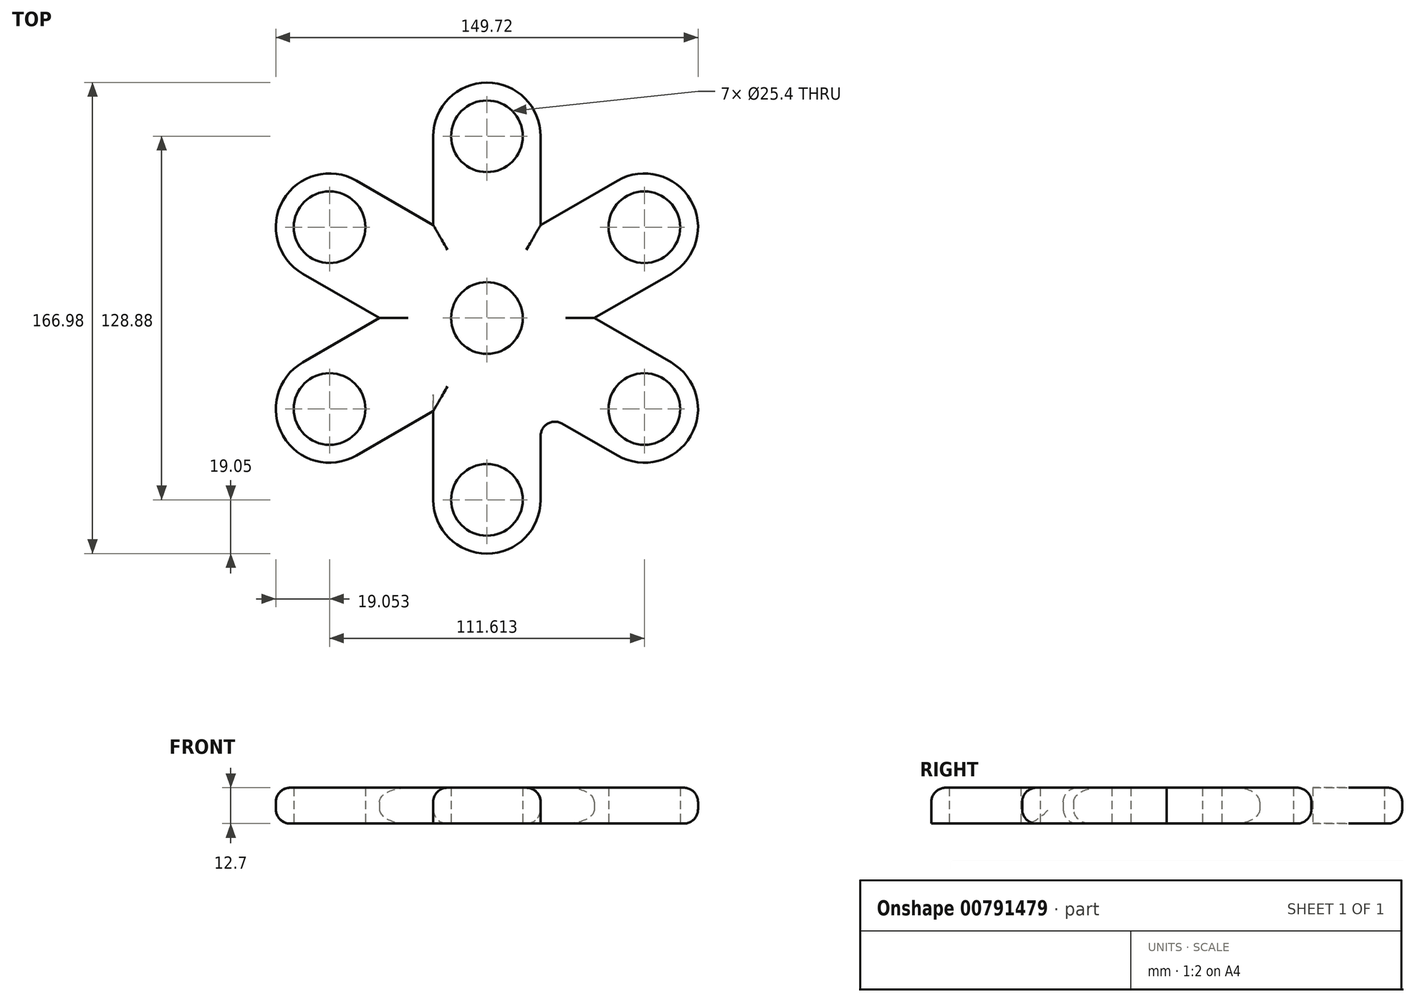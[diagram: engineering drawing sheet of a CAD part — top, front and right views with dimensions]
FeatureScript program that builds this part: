
annotation { "Feature Type Name" : "Feature", "Feature Type Description" : "" }
export const myFeature = defineFeature(function(context is Context, id is Id, definition is map)
    precondition{}
    {
        {
            var Q0;
            Q0=qCreatedBy(makeId("Top.planeOp"),FACE);
            var sketch = newSketch(context, id + "F0", { "sketchPlane" : qUnion([Q0])});
            skCircle(sketch, "E0", {"center": v(0, 0) * mm, "radius": 12.7 * mm});
            skCircle(sketch, "E1", {"center": v(0, 0) * mm, "radius": 19.05 * mm});
            skCircle(sketch, "E2", {"center": v(0, 64.44) * mm, "radius": 19.05 * mm});
            skCircle(sketch, "E3", {"center": v(0, 64.44) * mm, "radius": 12.7 * mm});
            skLineSegment(sketch, "E4", {"start": v(-19.05, 64.44) * mm, "end": v(-19.05, 0) * mm});
            skLineSegment(sketch, "E5", {"start": v(19.05, 64.44) * mm, "end": v(19.05, 0) * mm});
            skCircle(sketch, "E6.1.0", {"center": v(-55.8, 32.22) * mm, "radius": 12.7 * mm});
            skCircle(sketch, "E6.1.1", {"center": v(-55.8, 32.22) * mm, "radius": 19.05 * mm});
            skLineSegment(sketch, "E6.1.2", {"start": v(-46.28, 48.72) * mm, "end": v(9.53, 16.5) * mm});
            skLineSegment(sketch, "E6.1.3", {"start": v(-65.33, 15.72) * mm, "end": v(-9.52, -16.5) * mm});
            skCircle(sketch, "E6.2.0", {"center": v(-55.8, -32.22) * mm, "radius": 12.7 * mm});
            skCircle(sketch, "E6.2.1", {"center": v(-55.8, -32.22) * mm, "radius": 19.05 * mm});
            skLineSegment(sketch, "E6.2.2", {"start": v(-65.33, -15.72) * mm, "end": v(-9.52, 16.5) * mm});
            skLineSegment(sketch, "E6.2.3", {"start": v(-46.28, -48.72) * mm, "end": v(9.53, -16.5) * mm});
            skCircle(sketch, "E6.3.0", {"center": v(0, -64.44) * mm, "radius": 12.7 * mm});
            skCircle(sketch, "E6.3.1", {"center": v(0, -64.44) * mm, "radius": 19.05 * mm});
            skLineSegment(sketch, "E6.3.2", {"start": v(-19.05, -64.44) * mm, "end": v(-19.05, 0) * mm});
            skLineSegment(sketch, "E6.3.3", {"start": v(19.05, -64.44) * mm, "end": v(19.05, 0) * mm});
            skCircle(sketch, "E6.4.0", {"center": v(55.8, -32.22) * mm, "radius": 12.7 * mm});
            skCircle(sketch, "E6.4.1", {"center": v(55.8, -32.22) * mm, "radius": 19.05 * mm});
            skLineSegment(sketch, "E6.4.2", {"start": v(46.28, -48.72) * mm, "end": v(-9.53, -16.5) * mm});
            skLineSegment(sketch, "E6.4.3", {"start": v(65.33, -15.72) * mm, "end": v(9.52, 16.5) * mm});
            skCircle(sketch, "E6.5.0", {"center": v(55.8, 32.22) * mm, "radius": 12.7 * mm});
            skCircle(sketch, "E6.5.1", {"center": v(55.8, 32.22) * mm, "radius": 19.05 * mm});
            skLineSegment(sketch, "E6.5.2", {"start": v(65.33, 15.72) * mm, "end": v(9.53, -16.5) * mm});
            skLineSegment(sketch, "E6.5.3", {"start": v(46.28, 48.72) * mm, "end": v(-9.53, 16.5) * mm});
            skSolve(sketch);
        }
        {
            var Q0;
            Q0=makeQuery(id+"F0.imprint","IMPRINT",FACE,{"disambiguationData":[TD([[makeQuery(id+"F0.imprint","IMPRINT",EDGE,{"derivedFrom":sQuery(id+"F0.wireOp",EDGE,"E6.1.0")}),-1.0]])]});
            var Q1;
            {var subQ5=sQuery(id+"F0.wireOp",EDGE,"E6.1.2");var subQ6=sQuery(id+"F0.wireOp",EDGE,"E4");var subQ7=makeQuery(id+"F0.imprint","INTERSECT",VERTEX,{"derivedFrom":[subQ6,subQ5]});Q1=makeQuery(id+"F0.imprint","IMPRINT",FACE,{"disambiguationData":[TD([[makeQuery(id+"F0.imprint","IMPRINT",EDGE,{"disambiguationData":[TD([[subQ7,-1.0]])],"derivedFrom":subQ6}),-1.0]])]});}
            var Q2;
            {var subQ0=sQuery(id+"F0.wireOp",EDGE,"E6.1.2");var subQ1=sQuery(id+"F0.wireOp",EDGE,"E4");var subQ2=makeQuery(id+"F0.imprint","INTERSECT",VERTEX,{"derivedFrom":[subQ1,subQ0]});Q2=makeQuery(id+"F0.imprint","IMPRINT",FACE,{"disambiguationData":[TD([[makeQuery(id+"F0.imprint","IMPRINT",EDGE,{"disambiguationData":[TD([[subQ2,-1.0]])],"derivedFrom":subQ1}),1.0]])]});}
            var Q3;
            {var subQ1=sQuery(id+"F0.wireOp",EDGE,"E4");var subQ5=sQuery(id+"F0.wireOp",EDGE,"E2");var subQ6=makeQuery(id+"F0.imprint","INTERSECT",VERTEX,{"derivedFrom":[subQ5,subQ1]});Q3=makeQuery(id+"F0.imprint","IMPRINT",FACE,{"disambiguationData":[TD([[makeQuery(id+"F0.imprint","IMPRINT",EDGE,{"disambiguationData":[TD([[subQ6,-1.0]])],"derivedFrom":subQ5}),-1.0]])]});}
            var Q4;
            Q4=makeQuery(id+"F0.imprint","IMPRINT",FACE,{"disambiguationData":[TD([[makeQuery(id+"F0.imprint","IMPRINT",EDGE,{"derivedFrom":sQuery(id+"F0.wireOp",EDGE,"E3")}),-1.0]])]});
            var Q5;
            {var subQ5=sQuery(id+"F0.wireOp",EDGE,"E5");var subQ7=sQuery(id+"F0.wireOp",EDGE,"E6.5.3");var subQ9=makeQuery(id+"F0.imprint","INTERSECT",VERTEX,{"derivedFrom":[subQ5,subQ7]});Q5=makeQuery(id+"F0.imprint","IMPRINT",FACE,{"disambiguationData":[TD([[makeQuery(id+"F0.imprint","IMPRINT",EDGE,{"disambiguationData":[TD([[subQ9,-1.0]])],"derivedFrom":subQ5}),1.0]])]});}
            var Q6;
            Q6=makeQuery(id+"F0.imprint","IMPRINT",FACE,{"disambiguationData":[TD([[makeQuery(id+"F0.imprint","IMPRINT",EDGE,{"derivedFrom":sQuery(id+"F0.wireOp",EDGE,"E6.5.0")}),-1.0]])]});
            var Q7;
            {var subQ0=sQuery(id+"F0.wireOp",EDGE,"E6.5.3");var subQ1=sQuery(id+"F0.wireOp",EDGE,"E5");var subQ2=makeQuery(id+"F0.imprint","INTERSECT",VERTEX,{"derivedFrom":[subQ1,subQ0]});Q7=makeQuery(id+"F0.imprint","IMPRINT",FACE,{"disambiguationData":[TD([[makeQuery(id+"F0.imprint","IMPRINT",EDGE,{"disambiguationData":[TD([[subQ2,-1.0]])],"derivedFrom":subQ1}),-1.0]])]});}
            var Q8;
            {var subQ0=sQuery(id+"F0.wireOp",EDGE,"E5");var subQ3=sQuery(id+"F0.wireOp",EDGE,"E6.4.3");var subQ5=makeQuery(id+"F0.imprint","INTERSECT",VERTEX,{"derivedFrom":[subQ0,subQ3]});Q8=makeQuery(id+"F0.imprint","IMPRINT",FACE,{"disambiguationData":[TD([[makeQuery(id+"F0.imprint","IMPRINT",EDGE,{"disambiguationData":[TD([[subQ5,-1.0]])],"derivedFrom":subQ0}),-1.0]])]});}
            var Q9;
            {var subQ0=sQuery(id+"F0.wireOp",EDGE,"E6.1.2");var subQ3=sQuery(id+"F0.wireOp",EDGE,"E6.5.3");var subQ5=makeQuery(id+"F0.imprint","INTERSECT",VERTEX,{"derivedFrom":[subQ0,subQ3]});Q9=makeQuery(id+"F0.imprint","IMPRINT",FACE,{"disambiguationData":[TD([[makeQuery(id+"F0.imprint","IMPRINT",EDGE,{"disambiguationData":[TD([[subQ5,-1.0]])],"derivedFrom":subQ0}),-1.0]])]});}
            var Q10;
            {var subQ0=sQuery(id+"F0.wireOp",EDGE,"E4");var subQ3=sQuery(id+"F0.wireOp",EDGE,"E6.2.2");var subQ5=makeQuery(id+"F0.imprint","INTERSECT",VERTEX,{"derivedFrom":[subQ0,subQ3]});Q10=makeQuery(id+"F0.imprint","IMPRINT",FACE,{"disambiguationData":[TD([[makeQuery(id+"F0.imprint","IMPRINT",EDGE,{"disambiguationData":[TD([[subQ5,-1.0]])],"derivedFrom":subQ0}),1.0]])]});}
            var Q11;
            Q11=makeQuery(id+"F0.imprint","IMPRINT",FACE,{"disambiguationData":[TD([[makeQuery(id+"F0.imprint","IMPRINT",EDGE,{"derivedFrom":sQuery(id+"F0.wireOp",EDGE,"E0")}),-1.0]])]});
            var Q12;
            {var subQ0=sQuery(id+"F0.wireOp",EDGE,"E6.3.2");var subQ3=sQuery(id+"F0.wireOp",EDGE,"E6.1.3");var subQ5=makeQuery(id+"F0.imprint","INTERSECT",VERTEX,{"derivedFrom":[subQ3,subQ0]});Q12=makeQuery(id+"F0.imprint","IMPRINT",FACE,{"disambiguationData":[TD([[makeQuery(id+"F0.imprint","IMPRINT",EDGE,{"disambiguationData":[TD([[subQ5,-1.0]])],"derivedFrom":subQ3}),1.0]])]});}
            var Q13;
            {var subQ3=sQuery(id+"F0.wireOp",EDGE,"E6.2.2");var subQ5=sQuery(id+"F0.wireOp",EDGE,"E6.1.3");var subQ6=makeQuery(id+"F0.imprint","INTERSECT",VERTEX,{"derivedFrom":[subQ5,subQ3]});Q13=makeQuery(id+"F0.imprint","IMPRINT",FACE,{"disambiguationData":[TD([[makeQuery(id+"F0.imprint","IMPRINT",EDGE,{"disambiguationData":[TD([[subQ6,-1.0]])],"derivedFrom":subQ5}),1.0]])]});}
            var Q14;
            {var subQ5=sQuery(id+"F0.wireOp",EDGE,"E6.2.2");var subQ7=sQuery(id+"F0.wireOp",EDGE,"E6.1.3");var subQ9=makeQuery(id+"F0.imprint","INTERSECT",VERTEX,{"derivedFrom":[subQ7,subQ5]});Q14=makeQuery(id+"F0.imprint","IMPRINT",FACE,{"disambiguationData":[TD([[makeQuery(id+"F0.imprint","IMPRINT",EDGE,{"disambiguationData":[TD([[subQ9,-1.0]])],"derivedFrom":subQ7}),-1.0]])]});}
            var Q15;
            {var subQ3=sQuery(id+"F0.wireOp",EDGE,"E6.3.2");var subQ5=sQuery(id+"F0.wireOp",EDGE,"E6.2.3");var subQ6=makeQuery(id+"F0.imprint","INTERSECT",VERTEX,{"derivedFrom":[subQ5,subQ3]});Q15=makeQuery(id+"F0.imprint","IMPRINT",FACE,{"disambiguationData":[TD([[makeQuery(id+"F0.imprint","IMPRINT",EDGE,{"disambiguationData":[TD([[subQ6,-1.0]])],"derivedFrom":subQ5}),1.0]])]});}
            var Q16;
            {var subQ5=sQuery(id+"F0.wireOp",EDGE,"E6.3.2");var subQ7=sQuery(id+"F0.wireOp",EDGE,"E6.2.3");var subQ9=makeQuery(id+"F0.imprint","INTERSECT",VERTEX,{"derivedFrom":[subQ7,subQ5]});Q16=makeQuery(id+"F0.imprint","IMPRINT",FACE,{"disambiguationData":[TD([[makeQuery(id+"F0.imprint","IMPRINT",EDGE,{"disambiguationData":[TD([[subQ9,-1.0]])],"derivedFrom":subQ7}),-1.0]])]});}
            var Q17;
            {var subQ3=sQuery(id+"F0.wireOp",EDGE,"E6.4.2");var subQ5=sQuery(id+"F0.wireOp",EDGE,"E6.3.3");var subQ6=makeQuery(id+"F0.imprint","INTERSECT",VERTEX,{"derivedFrom":[subQ5,subQ3]});Q17=makeQuery(id+"F0.imprint","IMPRINT",FACE,{"disambiguationData":[TD([[makeQuery(id+"F0.imprint","IMPRINT",EDGE,{"disambiguationData":[TD([[subQ6,-1.0]])],"derivedFrom":subQ5}),1.0]])]});}
            var Q18;
            {var subQ5=sQuery(id+"F0.wireOp",EDGE,"E6.4.2");var subQ7=sQuery(id+"F0.wireOp",EDGE,"E6.3.3");var subQ9=makeQuery(id+"F0.imprint","INTERSECT",VERTEX,{"derivedFrom":[subQ7,subQ5]});Q18=makeQuery(id+"F0.imprint","IMPRINT",FACE,{"disambiguationData":[TD([[makeQuery(id+"F0.imprint","IMPRINT",EDGE,{"disambiguationData":[TD([[subQ9,-1.0]])],"derivedFrom":subQ7}),-1.0]])]});}
            var Q19;
            {var subQ3=sQuery(id+"F0.wireOp",EDGE,"E6.4.3");var subQ5=sQuery(id+"F0.wireOp",EDGE,"E6.5.2");var subQ6=makeQuery(id+"F0.imprint","INTERSECT",VERTEX,{"derivedFrom":[subQ3,subQ5]});Q19=makeQuery(id+"F0.imprint","IMPRINT",FACE,{"disambiguationData":[TD([[makeQuery(id+"F0.imprint","IMPRINT",EDGE,{"disambiguationData":[TD([[subQ6,-1.0]])],"derivedFrom":subQ3}),1.0]])]});}
            var Q20;
            {var subQ0=sQuery(id+"F0.wireOp",EDGE,"E6.3.3");var subQ3=sQuery(id+"F0.wireOp",EDGE,"E6.5.2");var subQ5=makeQuery(id+"F0.imprint","INTERSECT",VERTEX,{"derivedFrom":[subQ0,subQ3]});Q20=makeQuery(id+"F0.imprint","IMPRINT",FACE,{"disambiguationData":[TD([[makeQuery(id+"F0.imprint","IMPRINT",EDGE,{"disambiguationData":[TD([[subQ5,-1.0]])],"derivedFrom":subQ0}),1.0]])]});}
            var Q21;
            {var subQ0=sQuery(id+"F0.wireOp",EDGE,"E6.4.2");var subQ3=sQuery(id+"F0.wireOp",EDGE,"E6.2.3");var subQ5=makeQuery(id+"F0.imprint","INTERSECT",VERTEX,{"derivedFrom":[subQ3,subQ0]});Q21=makeQuery(id+"F0.imprint","IMPRINT",FACE,{"disambiguationData":[TD([[makeQuery(id+"F0.imprint","IMPRINT",EDGE,{"disambiguationData":[TD([[subQ5,-1.0]])],"derivedFrom":subQ3}),1.0]])]});}
            var Q22;
            Q22=makeQuery(id+"F0.imprint","IMPRINT",FACE,{"disambiguationData":[TD([[makeQuery(id+"F0.imprint","IMPRINT",EDGE,{"derivedFrom":sQuery(id+"F0.wireOp",EDGE,"E6.2.0")}),-1.0]])]});
            var Q23;
            Q23=makeQuery(id+"F0.imprint","IMPRINT",FACE,{"disambiguationData":[TD([[makeQuery(id+"F0.imprint","IMPRINT",EDGE,{"derivedFrom":sQuery(id+"F0.wireOp",EDGE,"E6.3.0")}),-1.0]])]});
            var Q24;
            Q24=makeQuery(id+"F0.imprint","IMPRINT",FACE,{"disambiguationData":[TD([[makeQuery(id+"F0.imprint","IMPRINT",EDGE,{"derivedFrom":sQuery(id+"F0.wireOp",EDGE,"E6.4.0")}),-1.0]])]});
            extrude(context, id + "F1", {"entities" : qUnion([Q0, Q1, Q2, Q3, Q4, Q5, Q6, Q7, Q8, Q9, Q10, Q11, Q12, Q13, Q14, Q15, Q16, Q17, Q18, Q19, Q20, Q21, Q22, Q23, Q24]), "depth" : 12.7 * mm, "offsetDistance" : 25.4 * mm});
        }
        {
            var Q0;
            Q0=makeQuery(id+"F1.opExtrude","CAP_EDGE",EDGE,{"disambiguationData":[OSD([sQuery(id+"F0.wireOp",EDGE,"E6.5.2")])],"isStart":false});
            var Q1;
            Q1=makeQuery(id+"F1.opExtrude","CAP_EDGE",EDGE,{"disambiguationData":[OSD([sQuery(id+"F0.wireOp",EDGE,"E5")])],"isStart":false});
            var Q2;
            Q2=makeQuery(id+"F1.opExtrude","CAP_EDGE",EDGE,{"disambiguationData":[OSD([sQuery(id+"F0.wireOp",EDGE,"E6.1.2")])],"isStart":false});
            var Q3;
            Q3=makeQuery(id+"F1.opExtrude","CAP_EDGE",EDGE,{"disambiguationData":[OSD([sQuery(id+"F0.wireOp",EDGE,"E6.2.2")])],"isStart":false});
            var Q4;
            Q4=makeQuery(id+"F1.opExtrude","CAP_EDGE",EDGE,{"disambiguationData":[OSD([sQuery(id+"F0.wireOp",EDGE,"E6.3.2")])],"isStart":false});
            var Q5;
            Q5=makeQuery(id+"F1.opExtrude","CAP_EDGE",EDGE,{"disambiguationData":[OSD([sQuery(id+"F0.wireOp",EDGE,"E6.4.2")])],"isStart":false});
            var Q6;
            Q6=makeQuery(id+"F1.opExtrude","SWEPT_FACE",FACE,{"disambiguationData":[OSD([sQuery(id+"F0.wireOp",EDGE,"E6.4.2")])]});
            var Q7;
            Q7=makeQuery(id+"F1.opExtrude","CAP_EDGE",EDGE,{"disambiguationData":[OSD([sQuery(id+"F0.wireOp",EDGE,"E6.2.2")])],"isStart":true});
            var Q8;
            Q8=makeQuery(id+"F1.opExtrude","CAP_EDGE",EDGE,{"disambiguationData":[OSD([sQuery(id+"F0.wireOp",EDGE,"E6.5.3")])],"isStart":true});
            var Q9;
            Q9=makeQuery(id+"F1.opExtrude","CAP_EDGE",EDGE,{"disambiguationData":[OSD([sQuery(id+"F0.wireOp",EDGE,"E6.1.3")])],"isStart":true});
            var Q10;
            Q10=makeQuery(id+"F1.opExtrude","CAP_EDGE",EDGE,{"disambiguationData":[OSD([sQuery(id+"F0.wireOp",EDGE,"E4")])],"isStart":true});
            fillet(context, id + "F2", {"entities" : qUnion([Q0, Q1, Q2, Q3, Q4, Q5, Q6, Q7, Q8, Q9, Q10]), "radius" : 5.08 * mm, "tangentPropagation" : true, "allowEdgeOverflow" : false});
        }
    });
